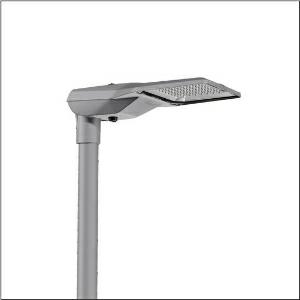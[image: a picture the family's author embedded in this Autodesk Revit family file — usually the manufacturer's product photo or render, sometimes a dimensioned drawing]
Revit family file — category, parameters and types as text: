
# Revit family: streetlight_sl_21_midi___st0_5a_5xe3b43t08nb_31ab
name_source: partatom
category: Lighting Fixtures
units: mm (PartAtom-declared; Revit-internal decimal feet)

## family parameters
Cut with Voids When Loaded = No
Host = Face
Light Source = No
Part Type = Normal
Room Calculation Point = No
Round Connector Dimension = Use Diameter
Shared = No

## types (1)
- --- (1 x LED, 23710 lm, 151.2 W, 4000K)
    Apparent Load = 151 VA
    CIE Flux Codes = 43 76 97 100 100
    Color Rendering = 70
    Color Temperature = 4000K
    Default Elevation = 1800 mm
    Description = Streetlight SL 21 midi, mast luminaire, primary light control with lens, of PMMA, primary optical cover: cover, of toughened safety glass, transparent, light distribution: ST0.5a, light emission: direct distribution, primary light characteristic: asymmetric, installation type: side-entry, post-top, LED, High Power LED, rated luminous flux: 23.710lm, luminous efficacy: 157lm/W, light colour: 740, colour temperature: 4000K, control gear: D4i, control: overheat protection, constant luminous flux control, time-dependent luminous flux control, flexible luminous flux parameterisation, pre-setting: logarithmic dimming characteristic, mains connection: 230..240V, AC, 50/60Hz, start of lifetime: 151W, end of service life: 157W, reduction: 70W, luminaire housing, of diecast aluminium, powder-coated, SITECO metallic grey (DB 702S), corrosivity category C5 high according to DIN EN ISO 12944, please order mast flange separately, inclination adjustable: 0°, 5°, 10°, 15°, sealing non-destructively replaceable, multi-level sealing system, length: 644mm, width: 335mm, height: 110mm, mast flange for spigot size: 42mm (side-entry): 5XC10008XM4, 60/48mm (side-entry/post-top): 5XC10108XM2, 76/60mm (side-entry/post-top): 5XC10108XM1, mounting height: 4..8m, Smart Interface below and above, protection rating (complete): IP66, insulation class (complete): insulation class II (safety insulation), certification: CE, ENEC, ENEC+, VDE, impact resistance: IK10, permissible operating ambient temperature for outdoor applications: -40..+50°C, standard-compliant lighting for roads and squares, packaging unit: 1 piece

Light Distribution: ST0.5a
    Height = 111 mm
    Lamp = 1 x LED
    Lamp Light Flux = 23710 lm
    Lamp Power = 151.2 W
    Lamp count = 1
    Length = 644 mm
    Luminous efficacy = 157 lm/W
    Manufacturer = Siteco
    ModVariant = No
    Model = 5XE3B43T08NB
    Number of Poles = 1
    OnlyDefault = Yes
    Power Factor = 1
    Product Name = Streetlight SL 21 midi | ST0.5a
    Product group = mast luminaire | pylon top
    ProductGroupID = 6100
    Protection Class = Protection class II
    Protection Degree = IP 66
    RLX_Detail_Level = 1
    RLX_Emergency_Light_Flux = 0 lm
    RLX_Emergency_Type = 0
    RLX_Emergency_Type_DB = No
    RlxData = <blob elided: 38261 chars, md5=9a9c0cc0>
    Socket = socket
    Standby Power = 0 W
    System Light Flux = 23710 lm
    System Power = 151 W
    Type Comments = factory setting: luminous flux: 100 % | dim-lin: 254 | 802 mA
    Type Image = l_1004304.jpg
    URL = http://relux.com
    VarID = @adj_170791
    Voltage = 0 V
    Weight = 0.00 kg
    Width = 336 mm

## geometry (parser evidence)
native form markers: Blend x4, Sweep x9
no freeform markers — native parametric forms only
